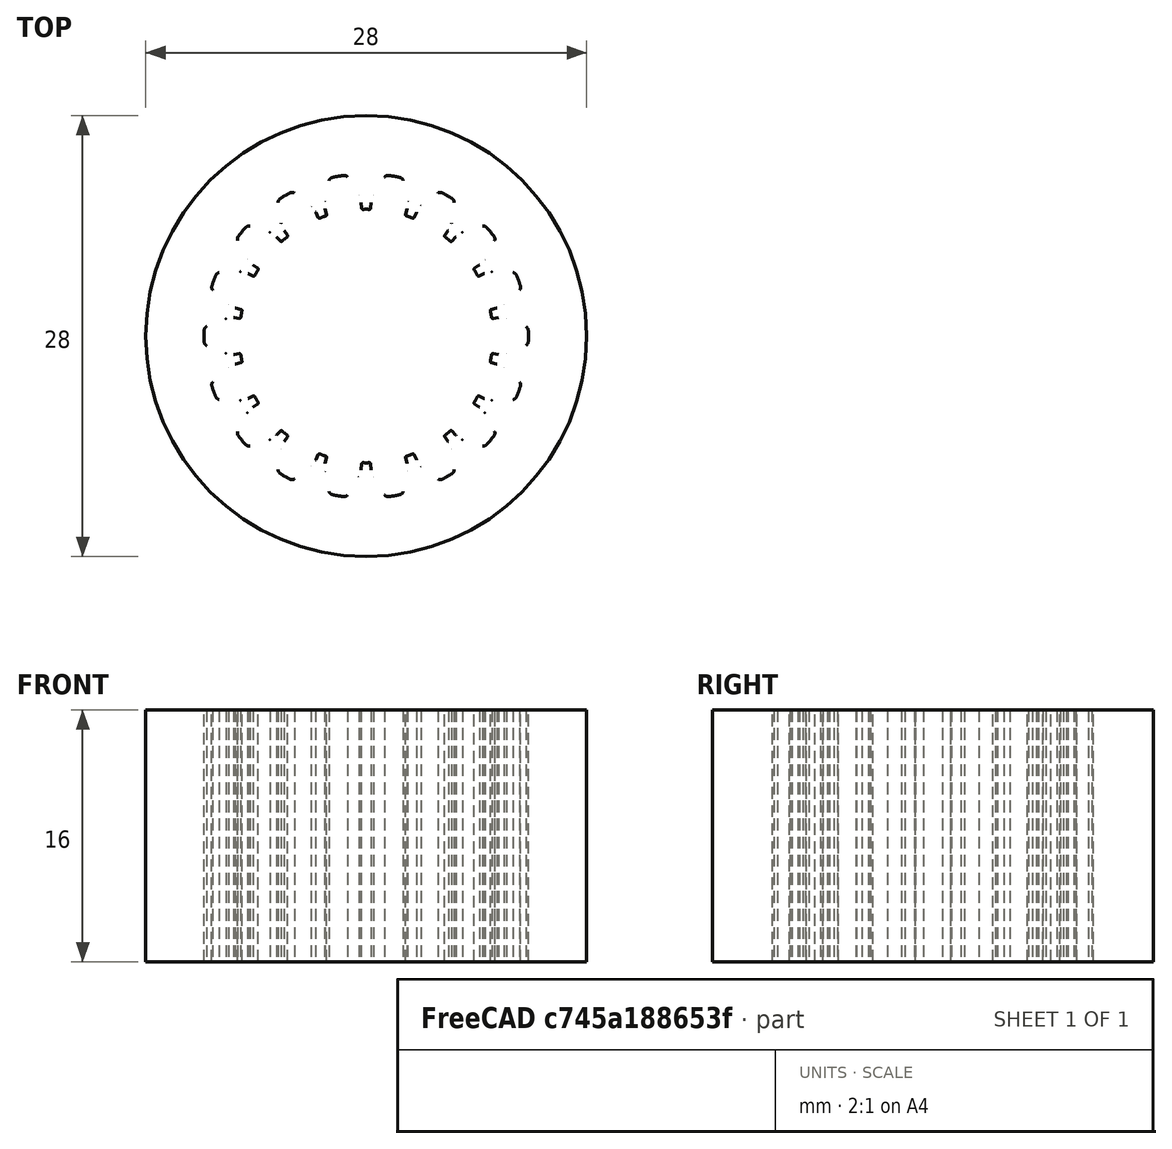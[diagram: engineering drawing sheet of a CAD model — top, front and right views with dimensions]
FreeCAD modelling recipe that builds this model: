
FCSTD DOCUMENT  (FreeCAD 0.19R24276 (Git))
Label: Gear_privod_perehodnik_to_GT2_gear_part_offset_3_d28_h16_A2
License: All rights reserved
LicenseURL: http://en.wikipedia.org/wiki/All_rights_reserved
objects: Part::Part2DObjectPython×1, Part::Offset2D×1, Part::FeaturePython×1
note: 3 computed .brp shape members not serialized (recipe doc carries the construction recipe); baked Part::Feature solids carry a one-line shape summary decoded from their .brp

FEATURE [Part::Part2DObjectPython] InvoluteGear  # Draft 2D object (typed FeaturePython)
  ExternalGear = true
  HighPrecision = true
  Modules = 1
  NumberOfTeeth = 18
  PressureAngle = 20
FEATURE [Part::Offset2D] Offset2D
  Fill = false
  Intersection = false
  Join = 0
  Mode = 1
  SelfIntersection = false
  Source = -> InvoluteGear
  Value = 0.3
FEATURE [Part::FeaturePython] b_Gear_privod_perehodnik_to_GT2_gear_part_offset_3_d28_h16_001_  label="Gear_privod_perehodnik_to_GT2_gear_part_offset_3_d28_h16_001"  # a2plus imported part (geometry in sourceFile) (typed FeaturePython)
  a2p_Version = V0.1
  fixedPosition = true
  objectType = a2pPart
  sourceFile = .\Gear_privod_perehodnik_to_GT2_gear_part_offset_3_d28_h16.FCStd
  subassemblyImport = false
  timeLastImport = 1.64791e+09
  updateColors = true
